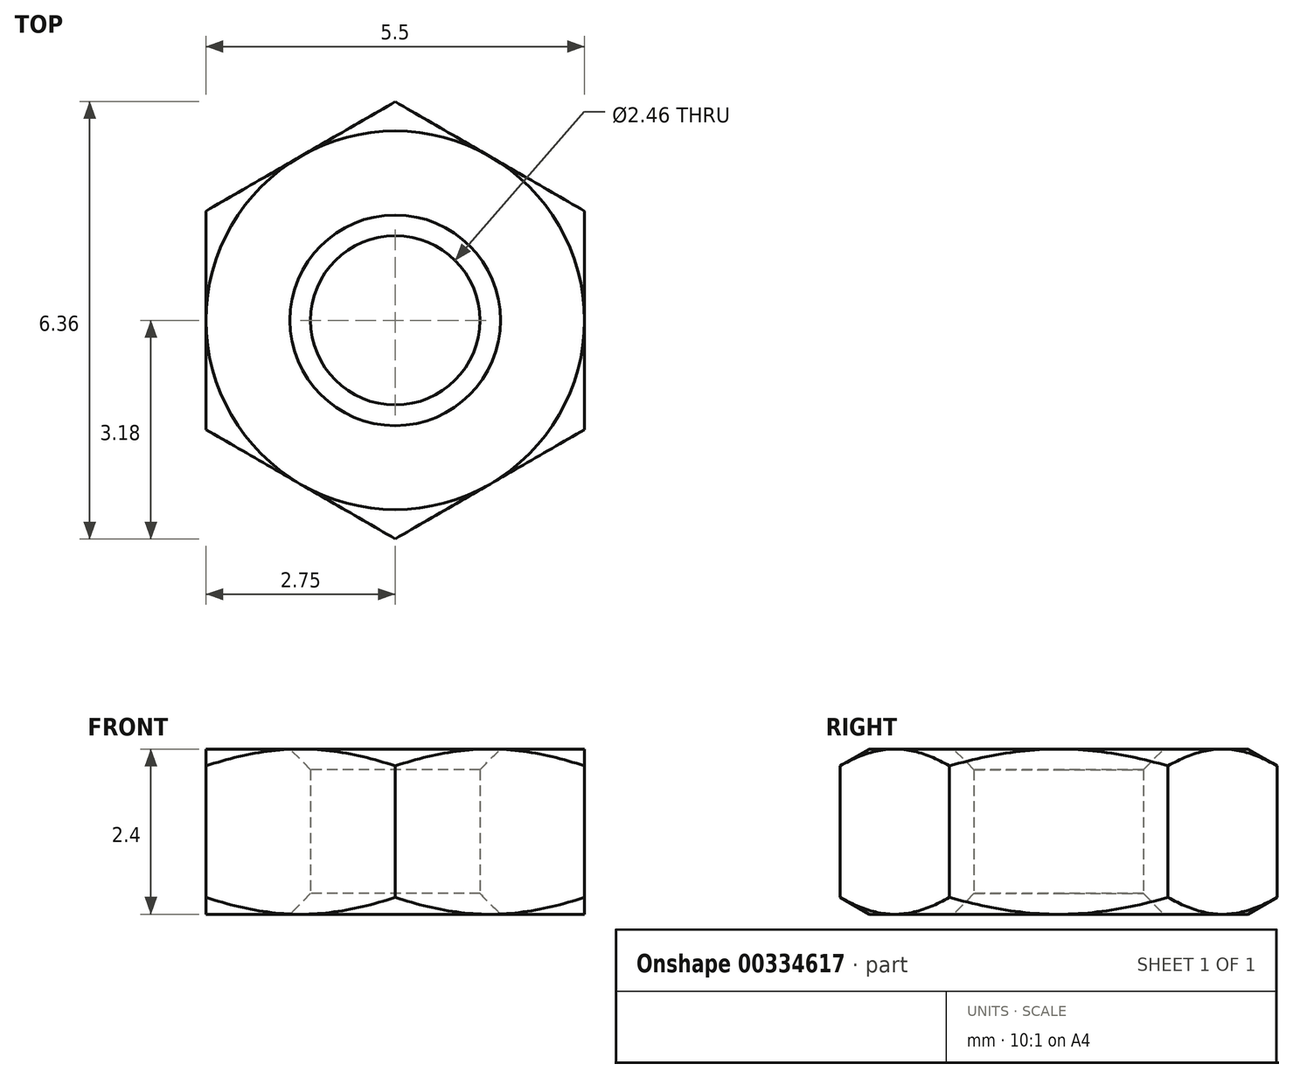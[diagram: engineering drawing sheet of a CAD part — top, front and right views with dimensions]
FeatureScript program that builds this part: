
annotation { "Feature Type Name" : "Feature", "Feature Type Description" : "" }
export const myFeature = defineFeature(function(context is Context, id is Id, definition is map)
    precondition{}
    {
        {
            var Q0;
            Q0=qCreatedBy(makeId("Top.planeOp"),FACE);
            var sketch = newSketch(context, id + "F0", { "sketchPlane" : qUnion([Q0])});
            skCircle(sketch, "E0.cCircle", {"center": v(0, 0) * mm, "radius": 2.75 * mm, "construction": true});
            skLineSegment(sketch, "E0.0", {"start": v(2.75, 1.59) * mm, "end": v(2.75, -1.59) * mm});
            skLineSegment(sketch, "E0.1", {"start": v(2.75, -1.59) * mm, "end": v(0, -3.18) * mm});
            skLineSegment(sketch, "E0.2", {"start": v(0, -3.18) * mm, "end": v(-2.75, -1.59) * mm});
            skLineSegment(sketch, "E0.3", {"start": v(-2.75, -1.59) * mm, "end": v(-2.75, 1.59) * mm});
            skLineSegment(sketch, "E0.4", {"start": v(-2.75, 1.59) * mm, "end": v(0, 3.18) * mm});
            skLineSegment(sketch, "E0.5", {"start": v(0, 3.18) * mm, "end": v(2.75, 1.59) * mm});
            skPoint(sketch, "E0.0.midPoint", {"position": v(2.75, 0) * mm});
            skCircle(sketch, "E1", {"center": v(0, 0) * mm, "radius": 1.23 * mm});
            skSolve(sketch);
        }
        {
            var Q0;
            Q0=qSketchRegion(id+"F0",true);
            extrude(context, id + "F1", {"entities" : qUnion([Q0]), "depth" : 2.4 * mm});
        }
        {
            var Q0;
            Q0=qCreatedBy(makeId("Front.planeOp"),FACE);
            var sketch = newSketch(context, id + "F2", { "sketchPlane" : qUnion([Q0])});
            skLineSegment(sketch, "E2.0", {"start": v(2.75, 2.4) * mm, "end": v(2.75, 0) * mm, "construction": true});
            skLineSegment(sketch, "E3", {"start": v(2.75, 2.4) * mm, "end": v(4.83, 2.4) * mm});
            skLineSegment(sketch, "E4", {"start": v(4.83, 2.4) * mm, "end": v(4.83, 0) * mm});
            skLineSegment(sketch, "E5", {"start": v(4.83, 0) * mm, "end": v(2.75, 0) * mm});
            skLineSegment(sketch, "E6", {"start": v(2.75, 2.4) * mm, "end": v(4.83, 1.2) * mm});
            skLineSegment(sketch, "E7", {"start": v(4.83, 1.2) * mm, "end": v(2.75, 0) * mm});
            skLineSegment(sketch, "E8", {"start": v(0, 0) * mm, "end": v(0, 2.35) * mm, "construction": true});
            skSolve(sketch);
        }
        {
            var Q0;
            Q0=qSketchRegion(id+"F2",true);
            var Q1;
            Q1=sQuery(id+"F2.wireOp",EDGE,"E8");
            revolve(context, id + "F3", {"operationType" : NewBodyOperationType.REMOVE, "entities" : qUnion([Q0]), "axis" : qUnion([Q1]), "revolveType" : RevolveType.FULL, "oppositeDirection" : true});
        }
        {
            var Q0;
            Q0=makeQuery(id+"F1.opExtrude","SWEPT_FACE",FACE,{"disambiguationData":[OSD([sQuery(id+"F0.wireOp",EDGE,"E1")])]});
            chamfer(context, id + "F4", {"entities" : qUnion([Q0]), "width" : 0.3 * mm, "tangentPropagation" : true});
        }
    });
